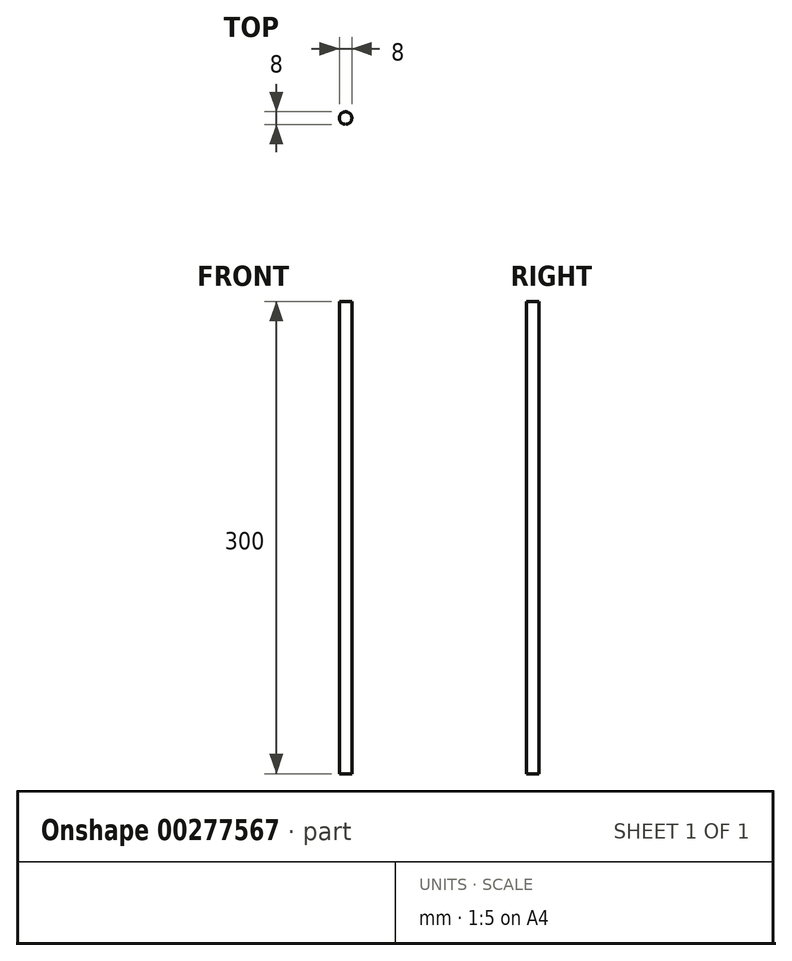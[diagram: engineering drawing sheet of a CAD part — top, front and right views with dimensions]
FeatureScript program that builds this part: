
annotation { "Feature Type Name" : "Feature", "Feature Type Description" : "" }
export const myFeature = defineFeature(function(context is Context, id is Id, definition is map)
    precondition{}
    {
        {
            var Q0;
            Q0=qCreatedBy(makeId("Top.planeOp"),FACE);
            var sketch = newSketch(context, id + "F0", { "sketchPlane" : qUnion([Q0])});
            skCircle(sketch, "E0", {"center": v(0, 0) * mm, "radius": 4 * mm});
            skSolve(sketch);
        }
        {
            var Q0;
            Q0=makeQuery(id+"F0.imprint","IMPRINT",FACE,{"disambiguationData":[TD([[makeQuery(id+"F0.imprint","IMPRINT",EDGE,{"derivedFrom":sQuery(id+"F0.wireOp",EDGE,"E0")}),1.0]])]});
            extrude(context, id + "F1", {"entities" : qUnion([Q0]), "depth" : 300 * mm, "offsetDistance" : 25 * mm});
        }
    });
